# Revit family: Bathtub-American_Standard-Cambridge-246X.X02_Series
name_source: partatom
category: Plumbing Fixtures
units: mm (PartAtom-declared; Revit-internal decimal feet)

## family parameters
Always vertical = No
Cut with Voids When Loaded = No
OmniClass Number = 23.45.05.14.21.11
OmniClass Title = Bath/Shower Units
Part Type = Normal
Room Calculation Point = No
Round Connector Dimension = Use Radius
Shared = Yes
Work Plane-Based = Yes

## types (6) — shared parameters
ADA Compliant = Yes
ANSI A117.1 = Yes
ASME A112.19.4M for Americast Fixtures = Yes
ASTM E162 for Flammability = Yes
ASTM F-462 for Slip-resistant Bathing Facilities = Yes
Assembly Code = D2010510
CW Connection = Yes
CWFU = 3
Default Elevation = 0"
Description = Cambridge 5' Bathing Pool Americast Brand Engineered Material
HW Connection = Yes
HWFU = 3
Height = 17 3/4"
Length = 60"
Manufacturer = American Standard
NFPA 258 for Smoke Density = Yes
Product Documentation Link = https://americanstandard.box.com
Product Page URL = https://www.americanstandard-us.com
Revised Date = 12/01/2021
URL = http://www.americanstandard-us.com
Vent Connection = No
WFU = 4
Waste Connection = Yes
Waste Connection Diameter = 1 1/2"
Waste Connection Radius = 3/4"
Width = 32"

## per-type parameters (varying)
| type | Drain Location | Finish | Left Bathtub | Material | Model | Oveflow Extrusion Start | Overflow Extrusion End | Right Bathtub |
| 2461.002.011 | 52" | Americast-American Standard-011-Arctic | No | Americast-American Standard-011-Arctic | 2461.002.011 | 52" | 60" | Yes |
| 2460.002.020 | 8" | Americast-American Standard-020-White | Yes | Americast-American Standard-020-White | 2460.002.020 | 0" | 8" | No |
| 2460.002.222 | 8" | Americast-American Standard-222-Linen | Yes | Americast-American Standard-222-Linen | 2460.002.222 | 0" | 8" | No |
| 2461.002.020 | 52" | Americast-American Standard-020-White | No | Americast-American Standard-020-White | 2461.002.020 | 52" | 60" | Yes |
| 2460.002.011 | 8" | Americast-American Standard-011-Arctic | Yes | Americast-American Standard-011-Arctic | 2460.002.011 | 0" | 8" | No |
| 2461.002.222 | 52" | Americast-American Standard-222-Linen | No | Americast-American Standard-222-Linen | 2461.002.022 | 52" | 60" | Yes |

## geometry (parser evidence)
native form markers: Extrusion x2, Sweep x2
no freeform markers — native parametric forms only
